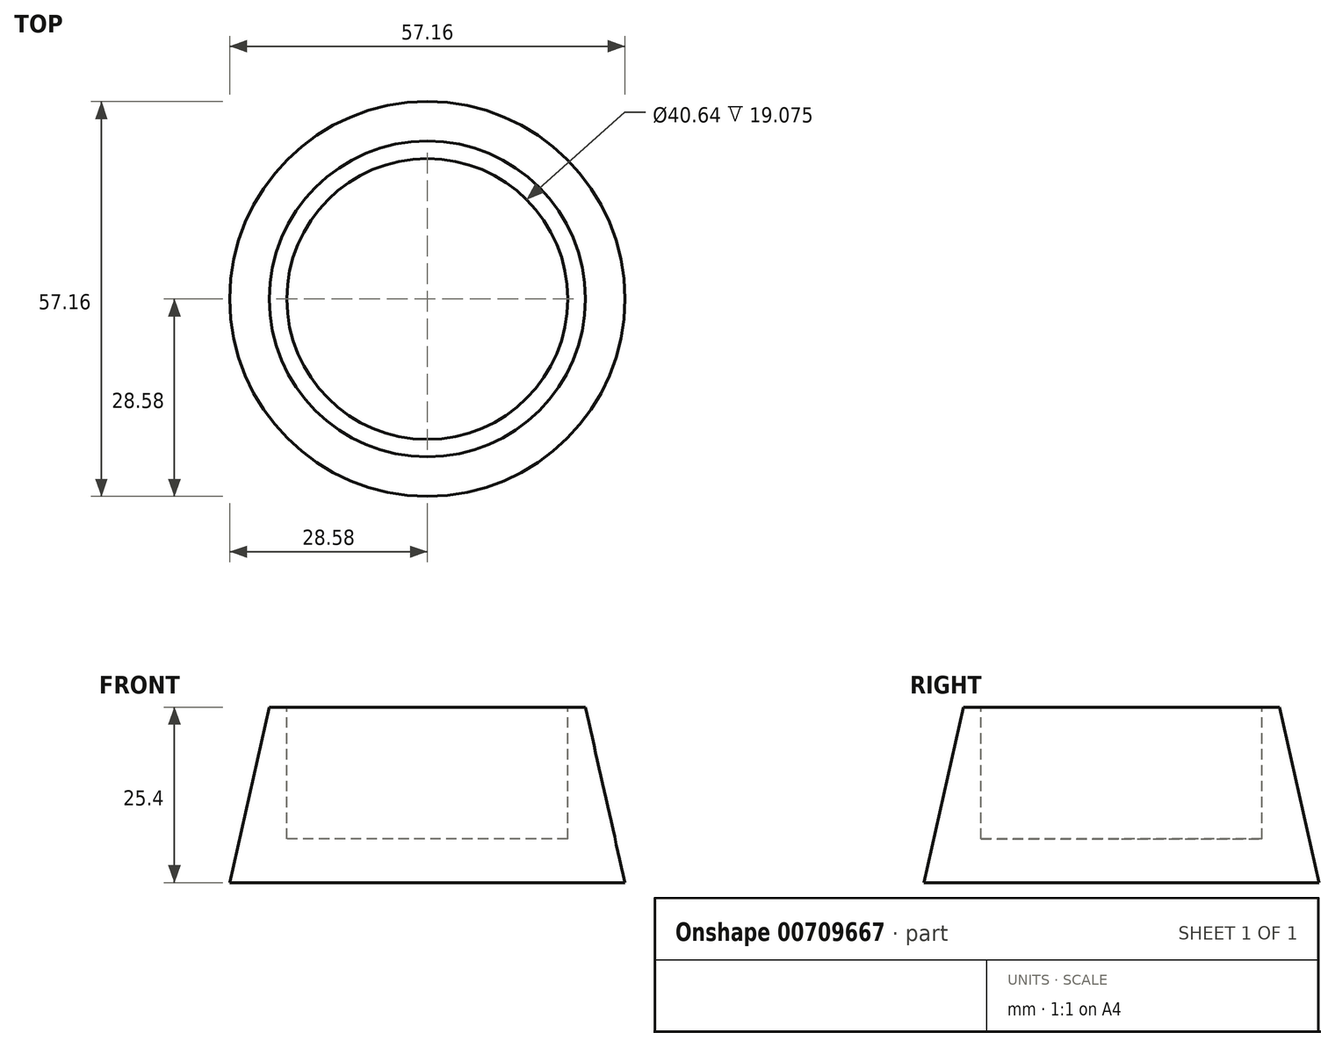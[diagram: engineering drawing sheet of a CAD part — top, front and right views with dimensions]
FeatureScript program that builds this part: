
annotation { "Feature Type Name" : "Feature", "Feature Type Description" : "" }
export const myFeature = defineFeature(function(context is Context, id is Id, definition is map)
    precondition{}
    {
        {
            var Q0;
            Q0=qCreatedBy(makeId("Top.planeOp"),FACE);
            var sketch = newSketch(context, id + "F0", { "sketchPlane" : qUnion([Q0])});
            skCircle(sketch, "E0", {"center": v(0, 0) * mm, "radius": 28.58 * mm});
            skSolve(sketch);
        }
        {
            var Q0;
            Q0=qCreatedBy(makeId("Top.planeOp"),FACE);
            cPlane(context, id + "F1", {"entities" : qUnion([Q0]), "cplaneType" : CPlaneType.OFFSET, "offset" : 25.4 * mm, "width" : 152.4 * mm, "height" : 152.4 * mm});
        }
        {
            var Q0;
            Q0=qCreatedBy(id+"F1.planeOp",FACE);
            var sketch = newSketch(context, id + "F2", { "sketchPlane" : qUnion([Q0])});
            skCircle(sketch, "E1", {"center": v(0, 0) * mm, "radius": 22.86 * mm});
            skSolve(sketch);
        }
        {
            var Q0;
            Q0=makeQuery(id+"F2.imprint","IMPRINT",FACE,{"disambiguationData":[TD([[makeQuery(id+"F2.imprint","IMPRINT",EDGE,{"derivedFrom":sQuery(id+"F2.wireOp",EDGE,"E1")}),1.0]])]});
            var Q1;
            Q1=makeQuery(id+"F0.imprint","IMPRINT",FACE,{"disambiguationData":[TD([[makeQuery(id+"F0.imprint","IMPRINT",EDGE,{"derivedFrom":sQuery(id+"F0.wireOp",EDGE,"E0")}),1.0]])]});
            loft(context, id + "F3", {"sheetProfilesArray" : [{ "sheetProfileEntities" : qUnion([Q0]) }, { "sheetProfileEntities" : qUnion([Q1]) }]});
        }
        {
            var Q0;
            Q0=qCreatedBy(id+"F1.planeOp",FACE);
            var sketch = newSketch(context, id + "F4", { "sketchPlane" : qUnion([Q0])});
            skCircle(sketch, "E2", {"center": v(0, 0) * mm, "radius": 20.32 * mm});
            skSolve(sketch);
        }
        {
            var Q0;
            Q0 = qSketchRegion(id + "F4", true);
            extrude(context, id + "F5", {"entities" : qUnion([Q0]), "operationType" : NewBodyOperationType.REMOVE, "oppositeDirection" : true, "depth" : 19.08 * mm, "offsetDistance" : 25.4 * mm});
        }
    });
